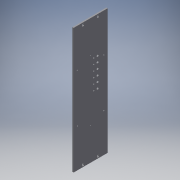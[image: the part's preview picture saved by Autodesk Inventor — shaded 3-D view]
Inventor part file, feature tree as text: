
AUTODESK INVENTOR PART (.ipt)
format: ipt  version: 2018 (Build 220112000, 112)  size: 217,088 bytes
history: native  units: mm
features: extrude x2, sketch x2
ambient origin geometry x8: Origin, YZ Plane, XZ Plane, XY Plane, X Axis, Y Axis, Z Axis, Center Point
bodies: Solid1 (feature_tree)
feature tree (4):
  extrude  "Extrusion1"  Depth=485.0mm
  extrude  "Extrusion2"  Depth=10.0mm
  sketch  "Sketch1"  dims[d0=132.0mm d1=485.0mm]
  sketch  "Sketch2"  dims[d2=5.0mm d3=0.0mm d4=10.48mm d7=28.87mm d10=234.34mm d11=5.24mm d12=6.93mm d13=20.0mm d15=468.68mm d16=20.0mm d18=57.74mm d21=242.0mm d22=85.0mm d23=117.9mm d24=42.5mm d25=3.3mm d26=20.0mm d28=235.8mm d29=10.0mm d31=10.0mm d33=117.9mm d34=8.1mm d35=5.0mm d37=15.0mm d38=18.0mm d39=15.0mm d40=4.05mm d41=7.1mm d42=60.0mm d44=22.0mm d45=10.0mm d47=10.0mm d49=5.0mm d50=0.0mm d51=452.563mm d52=452.563mm d53=7.42mm d54=15.08mm d55=187.0mm d56=4.2mm d57=8.0mm d58=4.2mm d59=8.0mm d61=20.0mm d63=20.0mm d65=20.0mm d67=10.0mm d69=60.0mm d71=10.0mm d72=15.08mm d73=187.0mm d74=4.2mm d76=4.2mm d78=7.42mm d79=8.0mm d80=8.0mm]
